# Revit family: SFSM Filter (Flange)
name_source: partatom
category: Mechanical Equipment
units: mm (PartAtom-declared; Revit-internal decimal feet)

## family parameters
Always vertical = Yes
Cut with Voids When Loaded = No
OmniClass Number = 23.65.50.11.11.11
OmniClass Title = Water Filters
Part Type = Normal
Room Calculation Point = No
Round Connector Dimension = Use Radius
Shared = No
Work Plane-Based = No

## types (3) — shared parameters
Assembly Code = D2090400
Black = Fluidra Base
Description = SFSM Series Vertical Sand Filter w/ Flanges
Fluidra_Description = SFSM Series Vertical Sand Filter w/ Flanges
Fluidra_Manufacturer = Fluidra
Fluidra_Max_Filtration_Rate = 20 gpm/ft²
Fluidra_Max_Working_Pressure = 50.00 psi
Fluidra_Number_of_Flange_Bolts = 4
Manufacturer = Fluidra
Tank = Fluidra Filter Body
URL = https://www.jandy.com

## per-type parameters (varying)
| type | Base | Base Diamter | Base Radius | Fluidra_Filter_Area | Fluidra_Freeboard | Fluidra_Max_Flow_Rate | Fluidra_Min_Backwash_Flow_Rate | Fluidra_Sand_Required | Fluidra_Six_Hour_Capacity | Fluidra_Weight (empty) | Height | Inlet Height (Center) | Outlet Height (Center) | Tank Bottom Height | Tank Diameter | Tank Radius Bottom | Tank Radius Top |
| SFSM100F | SFSM100 Base | 24 5/8" | 12 5/16" | 5.00 ft² | 15" | 100 GPM | 75 GPM | 679.00 lb | 36000.0 gal | 80.00 lb | 41" | 23 3/4" | 16" | 14 3/8" | 32 1/2" | 15 13/16" | 16 1/4" |
| SFSM120F | SFSM120-140 Base | 27 3/4" | 13 7/8" | 5.90 ft² | 13 1/2" | 118 GPM | 88 GPM | 1166.00 lb | 42480.0 gal | 147.00 lb | 47" | 26 3/8" | 18 5/8" | 17" | 35 1/2" | 17" | 17 3/4" |
| SFSM140F | SFSM120-140 Base | 27 3/4" | 13 7/8" | 7.06 ft² | 16" | 141 GPM | 105 GPM | 1256.00 lb | 50760.0 gal | 150.00 lb | 49 11/16" | 26 3/8" | 18 5/8" | 17" | 37 1/2" | 18" | 18 3/4" |

note: column(s) folded — value = type name in every type: Fluidra_Model, Model

## geometry (parser evidence)
native form markers: Sweep x17
no freeform markers — native parametric forms only
